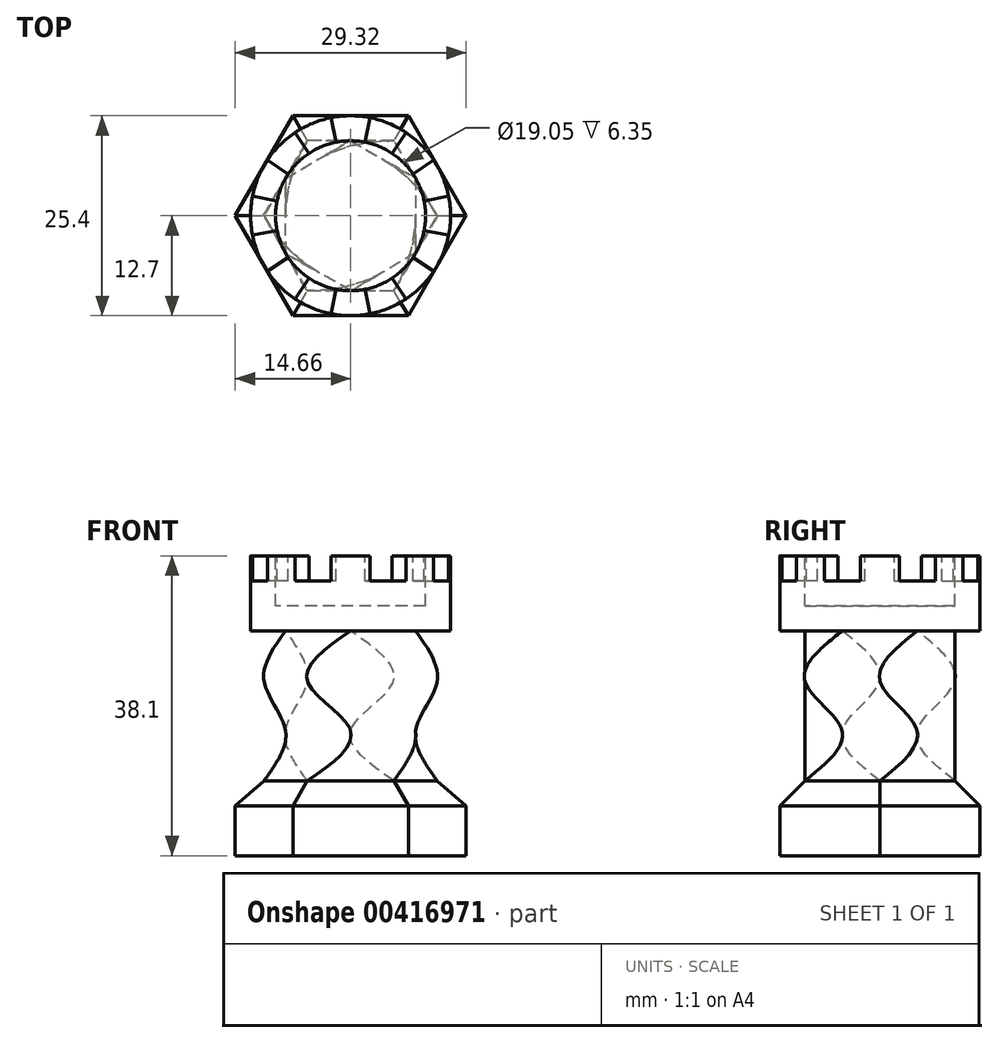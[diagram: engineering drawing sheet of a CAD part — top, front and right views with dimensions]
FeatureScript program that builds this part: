
annotation { "Feature Type Name" : "Feature", "Feature Type Description" : "" }
export const myFeature = defineFeature(function(context is Context, id is Id, definition is map)
    precondition{}
    {
        {
            var Q0;
            Q0=qCreatedBy(makeId("Top.planeOp"),FACE);
            var sketch = newSketch(context, id + "F0", { "sketchPlane" : qUnion([Q0])});
            skCircle(sketch, "E0.cCircle", {"center": v(0, 0) * mm, "radius": 12.7 * mm, "construction": true});
            skLineSegment(sketch, "E0.0", {"start": v(-7.33, 12.7) * mm, "end": v(7.33, 12.7) * mm});
            skLineSegment(sketch, "E0.1", {"start": v(7.33, 12.7) * mm, "end": v(14.66, 0) * mm});
            skLineSegment(sketch, "E0.2", {"start": v(14.66, 0) * mm, "end": v(7.33, -12.7) * mm});
            skLineSegment(sketch, "E0.3", {"start": v(7.33, -12.7) * mm, "end": v(-7.33, -12.7) * mm});
            skLineSegment(sketch, "E0.4", {"start": v(-7.33, -12.7) * mm, "end": v(-14.66, 0) * mm});
            skLineSegment(sketch, "E0.5", {"start": v(-14.66, 0) * mm, "end": v(-7.33, 12.7) * mm});
            skPoint(sketch, "E0.0.midPoint", {"position": v(0, 12.7) * mm});
            skSolve(sketch);
        }
        {
            var Q0;
            Q0=makeQuery(id+"F0.imprint","IMPRINT",FACE,{"disambiguationData":[TD([[makeQuery(id+"F0.imprint","IMPRINT",EDGE,{"derivedFrom":sQuery(id+"F0.wireOp",EDGE,"E0.0")}),-1.0]])]});
            extrude(context, id + "F1", {"entities" : qUnion([Q0]), "depth" : 9.52 * mm, "offsetDistance" : 25.4 * mm});
        }
        {
            var Q0;
            Q0=makeQuery(id+"F1.opExtrude","CAP_EDGE",EDGE,{"disambiguationData":[OSD([sQuery(id+"F0.wireOp",EDGE,"E0.3")])],"isStart":false});
            var Q1;
            Q1=makeQuery(id+"F1.opExtrude","CAP_EDGE",EDGE,{"disambiguationData":[OSD([sQuery(id+"F0.wireOp",EDGE,"E0.2")])],"isStart":false});
            var Q2;
            Q2=makeQuery(id+"F1.opExtrude","CAP_EDGE",EDGE,{"disambiguationData":[OSD([sQuery(id+"F0.wireOp",EDGE,"E0.1")])],"isStart":false});
            var Q3;
            Q3=makeQuery(id+"F1.opExtrude","CAP_EDGE",EDGE,{"disambiguationData":[OSD([sQuery(id+"F0.wireOp",EDGE,"E0.0")])],"isStart":false});
            var Q4;
            Q4=makeQuery(id+"F1.opExtrude","CAP_EDGE",EDGE,{"disambiguationData":[OSD([sQuery(id+"F0.wireOp",EDGE,"E0.5")])],"isStart":false});
            var Q5;
            Q5=makeQuery(id+"F1.opExtrude","CAP_EDGE",EDGE,{"disambiguationData":[OSD([sQuery(id+"F0.wireOp",EDGE,"E0.4")])],"isStart":false});
            chamfer(context, id + "F2", {"entities" : qUnion([Q0, Q1, Q2, Q3, Q4, Q5]), "width" : 3.17 * mm, "tangentPropagation" : true});
        }
        {
            var Q0;
            Q0=makeQuery(id+"F1.opExtrude","CAP_FACE",FACE,{"disambiguationData":[OSD([sQuery(id+"F0.wireOp",EDGE,"E0.0"),sQuery(id+"F0.wireOp",EDGE,"E0.1"),sQuery(id+"F0.wireOp",EDGE,"E0.2"),sQuery(id+"F0.wireOp",EDGE,"E0.3"),sQuery(id+"F0.wireOp",EDGE,"E0.4"),sQuery(id+"F0.wireOp",EDGE,"E0.5")])],"isStart":false});
            cPlane(context, id + "F3", {"entities" : qUnion([Q0]), "cplaneType" : CPlaneType.OFFSET, "offset" : 6.35 * mm, "width" : 152.4 * mm, "height" : 152.4 * mm});
        }
        {
            var Q0;
            Q0=qCreatedBy(id+"F3.planeOp",FACE);
            var sketch = newSketch(context, id + "F4", { "sketchPlane" : qUnion([Q0])});
            skCircle(sketch, "E1.cCircle", {"center": v(0, 0) * mm, "radius": 8.25 * mm, "construction": true});
            skLineSegment(sketch, "E1.0", {"start": v(8.25, -4.76) * mm, "end": v(0, -9.53) * mm});
            skLineSegment(sketch, "E1.1", {"start": v(0, -9.52) * mm, "end": v(-8.25, -4.76) * mm});
            skLineSegment(sketch, "E1.2", {"start": v(-8.25, -4.76) * mm, "end": v(-8.25, 4.76) * mm});
            skLineSegment(sketch, "E1.3", {"start": v(-8.25, 4.76) * mm, "end": v(0, 9.52) * mm});
            skLineSegment(sketch, "E1.4", {"start": v(0, 9.52) * mm, "end": v(8.25, 4.76) * mm});
            skLineSegment(sketch, "E1.5", {"start": v(8.25, 4.76) * mm, "end": v(8.25, -4.76) * mm});
            skPoint(sketch, "E1.0.midPoint", {"position": v(4.12, -7.14) * mm});
            skSolve(sketch);
        }
        {
            var Q0;
            Q0=makeQuery(id+"F4.imprint","IMPRINT",FACE,{"disambiguationData":[TD([[makeQuery(id+"F4.imprint","IMPRINT",EDGE,{"derivedFrom":sQuery(id+"F4.wireOp",EDGE,"E1.0")}),-1.0]])]});
            cPlane(context, id + "F5", {"entities" : qUnion([Q0]), "cplaneType" : CPlaneType.OFFSET, "offset" : 6.35 * mm, "width" : 152.4 * mm, "height" : 152.4 * mm});
        }
        {
            var Q0;
            Q0=qCreatedBy(id+"F5.planeOp",FACE);
            var sketch = newSketch(context, id + "F6", { "sketchPlane" : qUnion([Q0])});
            skCircle(sketch, "E2.cCircle", {"center": v(0, 0) * mm, "radius": 9.52 * mm, "construction": true});
            skLineSegment(sketch, "E2.0", {"start": v(-5.5, 9.52) * mm, "end": v(5.5, 9.52) * mm});
            skLineSegment(sketch, "E2.1", {"start": v(5.5, 9.53) * mm, "end": v(11, 0) * mm});
            skLineSegment(sketch, "E2.2", {"start": v(11, 0) * mm, "end": v(5.5, -9.53) * mm});
            skLineSegment(sketch, "E2.3", {"start": v(5.5, -9.52) * mm, "end": v(-5.5, -9.52) * mm});
            skLineSegment(sketch, "E2.4", {"start": v(-5.5, -9.53) * mm, "end": v(-11, 0) * mm});
            skLineSegment(sketch, "E2.5", {"start": v(-11, 0) * mm, "end": v(-5.5, 9.53) * mm});
            skPoint(sketch, "E2.0.midPoint", {"position": v(0, 9.52) * mm});
            skSolve(sketch);
        }
        {
            var Q0;
            Q0=makeQuery(id+"F6.imprint","IMPRINT",FACE,{"disambiguationData":[TD([[makeQuery(id+"F6.imprint","IMPRINT",EDGE,{"derivedFrom":sQuery(id+"F6.wireOp",EDGE,"E2.0")}),-1.0]])]});
            cPlane(context, id + "F7", {"entities" : qUnion([Q0]), "cplaneType" : CPlaneType.OFFSET, "offset" : 6.35 * mm, "width" : 152.4 * mm, "height" : 152.4 * mm});
        }
        {
            var Q0;
            Q0=qCreatedBy(id+"F7.planeOp",FACE);
            var sketch = newSketch(context, id + "F8", { "sketchPlane" : qUnion([Q0])});
            skCircle(sketch, "E3.cCircle", {"center": v(0, 0) * mm, "radius": 8.25 * mm, "construction": true});
            skLineSegment(sketch, "E3.0", {"start": v(-8.25, 4.76) * mm, "end": v(0, 9.53) * mm});
            skLineSegment(sketch, "E3.1", {"start": v(0, 9.52) * mm, "end": v(8.25, 4.76) * mm});
            skLineSegment(sketch, "E3.2", {"start": v(8.25, 4.76) * mm, "end": v(8.25, -4.76) * mm});
            skLineSegment(sketch, "E3.3", {"start": v(8.25, -4.76) * mm, "end": v(0, -9.53) * mm});
            skLineSegment(sketch, "E3.4", {"start": v(0, -9.53) * mm, "end": v(-8.25, -4.76) * mm});
            skLineSegment(sketch, "E3.5", {"start": v(-8.25, -4.76) * mm, "end": v(-8.25, 4.76) * mm});
            skPoint(sketch, "E3.0.midPoint", {"position": v(-4.12, 7.14) * mm});
            skSolve(sketch);
        }
        {
            var Q1;
            Q1=makeQuery(id+"F1.opExtrude","CAP_FACE",FACE,{"disambiguationData":[OSD([sQuery(id+"F0.wireOp",EDGE,"E0.0"),sQuery(id+"F0.wireOp",EDGE,"E0.1"),sQuery(id+"F0.wireOp",EDGE,"E0.2"),sQuery(id+"F0.wireOp",EDGE,"E0.3"),sQuery(id+"F0.wireOp",EDGE,"E0.4"),sQuery(id+"F0.wireOp",EDGE,"E0.5")])],"isStart":false});
            var Q2;
            Q2=makeQuery(id+"F4.imprint","IMPRINT",FACE,{"disambiguationData":[TD([[makeQuery(id+"F4.imprint","IMPRINT",EDGE,{"derivedFrom":sQuery(id+"F4.wireOp",EDGE,"E1.0")}),-1.0]])]});
            var Q3;
            Q3=makeQuery(id+"F6.imprint","IMPRINT",FACE,{"disambiguationData":[TD([[makeQuery(id+"F6.imprint","IMPRINT",EDGE,{"derivedFrom":sQuery(id+"F6.wireOp",EDGE,"E2.0")}),-1.0]])]});
            var Q4;
            Q4=makeQuery(id+"F8.imprint","IMPRINT",FACE,{"disambiguationData":[TD([[makeQuery(id+"F8.imprint","IMPRINT",EDGE,{"derivedFrom":sQuery(id+"F8.wireOp",EDGE,"E3.0")}),-1.0]])]});
            loft(context, id + "F9", {"operationType" : NewBodyOperationType.ADD, "sheetProfilesArray" : [{ "sheetProfileEntities" : qUnion([Q1]) }, { "sheetProfileEntities" : qUnion([Q2]) }, { "sheetProfileEntities" : qUnion([Q3]) }, { "sheetProfileEntities" : qUnion([Q4]) }]});
        }
        {
            var Q0;
            Q0=makeQuery(id+"F9.opLoft","CAP_FACE",FACE,{"disambiguationData":[OSD([makeQuery(id+"F8.imprint","IMPRINT",FACE,{"disambiguationData":[TD([[makeQuery(id+"F8.imprint","IMPRINT",EDGE,{"derivedFrom":sQuery(id+"F8.wireOp",EDGE,"E3.0")}),-1.0]])]})])],"isStart":true});
            var sketch = newSketch(context, id + "F10", { "sketchPlane" : qUnion([Q0])});
            skCircle(sketch, "E4", {"center": v(0, 0) * mm, "radius": 12.7 * mm});
            skCircle(sketch, "E5", {"center": v(0, 0) * mm, "radius": 9.53 * mm});
            skSolve(sketch);
        }
        {
            var Q0;
            Q0=makeQuery(id+"F10.imprint","IMPRINT",FACE,{"disambiguationData":[TD([[makeQuery(id+"F10.imprint","IMPRINT",EDGE,{"derivedFrom":sQuery(id+"F10.wireOp",EDGE,"E4")}),1.0]])]});
            var Q1;
            {var subQ2=sQuery(id+"F8.wireOp",EDGE,"E3.1");var subQ3=sQuery(id+"F8.wireOp",EDGE,"E3.0");var subQ4=sQuery(id+"F8.wireOp",EDGE,"E3.5");Q1=makeQuery(id+"F10.imprint","IMPRINT",FACE,{"disambiguationData":[TD([[makeQuery(id+"F10.imprint","IMPRINT",EDGE,{"derivedFrom":makeQuery(id+"F9.opLoft","MID_CAP_EDGE",EDGE,{"disambiguationData":[OSD([subQ3,subQ2,subQ4])],"capPos":3.0})}),1.0]])]});}
            var Q2;
            {var subQ1=sQuery(id+"F8.wireOp",EDGE,"E3.5");var subQ2=sQuery(id+"F8.wireOp",EDGE,"E3.0");var subQ3=sQuery(id+"F8.wireOp",EDGE,"E3.1");var subQ4=makeQuery(id+"F9.opLoft","MID_CAP_EDGE",EDGE,{"disambiguationData":[OSD([subQ2,subQ3,subQ1])],"capPos":3.0});Q2=makeQuery(id+"F10.imprint","IMPRINT",FACE,{"disambiguationData":[TD([[makeQuery(id+"F10.imprint","IMPRINT",EDGE,{"derivedFrom":subQ4}),-1.0]])]});}
            var Q3;
            {var subQ1=sQuery(id+"F8.wireOp",EDGE,"E3.2");var subQ2=sQuery(id+"F8.wireOp",EDGE,"E3.1");var subQ3=sQuery(id+"F8.wireOp",EDGE,"E3.0");var subQ4=makeQuery(id+"F9.opLoft","MID_CAP_EDGE",EDGE,{"disambiguationData":[OSD([subQ3,subQ2,subQ1])],"capPos":3.0});Q3=makeQuery(id+"F10.imprint","IMPRINT",FACE,{"disambiguationData":[TD([[makeQuery(id+"F10.imprint","IMPRINT",EDGE,{"derivedFrom":subQ4}),-1.0]])]});}
            var Q4;
            {var subQ1=sQuery(id+"F8.wireOp",EDGE,"E3.5");var subQ2=sQuery(id+"F8.wireOp",EDGE,"E3.4");var subQ3=sQuery(id+"F8.wireOp",EDGE,"E3.0");var subQ4=makeQuery(id+"F9.opLoft","MID_CAP_EDGE",EDGE,{"disambiguationData":[OSD([subQ3,subQ2,subQ1])],"capPos":3.0});Q4=makeQuery(id+"F10.imprint","IMPRINT",FACE,{"disambiguationData":[TD([[makeQuery(id+"F10.imprint","IMPRINT",EDGE,{"derivedFrom":subQ4}),-1.0]])]});}
            var Q5;
            {var subQ1=sQuery(id+"F8.wireOp",EDGE,"E3.5");var subQ2=sQuery(id+"F8.wireOp",EDGE,"E3.4");var subQ3=sQuery(id+"F8.wireOp",EDGE,"E3.3");var subQ4=makeQuery(id+"F9.opLoft","MID_CAP_EDGE",EDGE,{"disambiguationData":[OSD([subQ3,subQ2,subQ1])],"capPos":3.0});Q5=makeQuery(id+"F10.imprint","IMPRINT",FACE,{"disambiguationData":[TD([[makeQuery(id+"F10.imprint","IMPRINT",EDGE,{"derivedFrom":subQ4}),-1.0]])]});}
            var Q6;
            {var subQ1=sQuery(id+"F8.wireOp",EDGE,"E3.3");var subQ2=sQuery(id+"F8.wireOp",EDGE,"E3.2");var subQ3=sQuery(id+"F8.wireOp",EDGE,"E3.1");var subQ4=makeQuery(id+"F9.opLoft","MID_CAP_EDGE",EDGE,{"disambiguationData":[OSD([subQ3,subQ2,subQ1])],"capPos":3.0});Q6=makeQuery(id+"F10.imprint","IMPRINT",FACE,{"disambiguationData":[TD([[makeQuery(id+"F10.imprint","IMPRINT",EDGE,{"derivedFrom":subQ4}),-1.0]])]});}
            var Q7;
            {var subQ1=sQuery(id+"F8.wireOp",EDGE,"E3.4");var subQ2=sQuery(id+"F8.wireOp",EDGE,"E3.3");var subQ3=sQuery(id+"F8.wireOp",EDGE,"E3.2");var subQ4=makeQuery(id+"F9.opLoft","MID_CAP_EDGE",EDGE,{"disambiguationData":[OSD([subQ3,subQ2,subQ1])],"capPos":3.0});Q7=makeQuery(id+"F10.imprint","IMPRINT",FACE,{"disambiguationData":[TD([[makeQuery(id+"F10.imprint","IMPRINT",EDGE,{"derivedFrom":subQ4}),-1.0]])]});}
            extrude(context, id + "F11", {"entities" : qUnion([Q0, Q1, Q2, Q3, Q4, Q5, Q6, Q7]), "operationType" : NewBodyOperationType.ADD, "depth" : 9.52 * mm, "offsetDistance" : 25.4 * mm});
        }
        {
            var Q0;
            Q0=makeQuery(id+"F11.opExtrude","CAP_FACE",FACE,{"disambiguationData":[OSD([sQuery(id+"F10.wireOp",EDGE,"E4")])],"isStart":false});
            var sketch = newSketch(context, id + "F12", { "sketchPlane" : qUnion([Q0])});
            skCircle(sketch, "E6", {"center": v(0, 0) * mm, "radius": 9.53 * mm});
            skLineSegment(sketch, "E7", {"start": v(0, 0) * mm, "end": v(0, 12.7) * mm});
            skLineSegment(sketch, "E8", {"start": v(0, 0) * mm, "end": v(12.7, 0) * mm});
            skLineSegment(sketch, "E9", {"start": v(0, 0) * mm, "end": v(-12.7, 0) * mm});
            skLineSegment(sketch, "E10", {"start": v(0, 0) * mm, "end": v(0, -12.7) * mm});
            skLineSegment(sketch, "E11", {"start": v(0, 0) * mm, "end": v(-8.98, 8.98) * mm});
            skLineSegment(sketch, "E12", {"start": v(0, 0) * mm, "end": v(8.98, -8.98) * mm});
            skLineSegment(sketch, "E13", {"start": v(0, 0) * mm, "end": v(8.98, 8.98) * mm});
            skLineSegment(sketch, "E14", {"start": v(0, 0) * mm, "end": v(-8.98, -8.98) * mm});
            skLineSegment(sketch, "E15", {"start": v(0, 0) * mm, "end": v(-4.86, 11.73) * mm});
            skLineSegment(sketch, "E16", {"start": v(0, 0) * mm, "end": v(4.86, 11.73) * mm});
            skLineSegment(sketch, "E17", {"start": v(0, 0) * mm, "end": v(11.73, 4.86) * mm});
            skLineSegment(sketch, "E18", {"start": v(0, 0) * mm, "end": v(11.73, -4.86) * mm});
            skLineSegment(sketch, "E19", {"start": v(0, 0) * mm, "end": v(4.86, -11.73) * mm});
            skLineSegment(sketch, "E20", {"start": v(0, 0) * mm, "end": v(-4.86, -11.73) * mm});
            skLineSegment(sketch, "E21", {"start": v(0, 0) * mm, "end": v(-11.73, 4.86) * mm});
            skLineSegment(sketch, "E22", {"start": v(0, 0) * mm, "end": v(-11.73, -4.86) * mm});
            skLineSegment(sketch, "E23", {"start": v(0, 0) * mm, "end": v(-2.48, 12.46) * mm});
            skLineSegment(sketch, "E24", {"start": v(0, 0) * mm, "end": v(2.48, 12.46) * mm});
            skLineSegment(sketch, "E25", {"start": v(0, 0) * mm, "end": v(7.06, 10.56) * mm});
            skLineSegment(sketch, "E26", {"start": v(0, 0) * mm, "end": v(10.56, 7.06) * mm});
            skLineSegment(sketch, "E27", {"start": v(0, 0) * mm, "end": v(12.46, 2.48) * mm});
            skLineSegment(sketch, "E28", {"start": v(0, 0) * mm, "end": v(12.46, -2.48) * mm});
            skLineSegment(sketch, "E29", {"start": v(0, 0) * mm, "end": v(10.56, -7.06) * mm});
            skLineSegment(sketch, "E30", {"start": v(0, 0) * mm, "end": v(7.06, -10.56) * mm});
            skLineSegment(sketch, "E31", {"start": v(0, 0) * mm, "end": v(2.48, -12.46) * mm});
            skLineSegment(sketch, "E32", {"start": v(0, 0) * mm, "end": v(-7.06, 10.56) * mm});
            skLineSegment(sketch, "E33", {"start": v(0, 0) * mm, "end": v(-10.56, 7.06) * mm});
            skLineSegment(sketch, "E34", {"start": v(0, 0) * mm, "end": v(-12.46, 2.48) * mm});
            skLineSegment(sketch, "E35", {"start": v(0, 0) * mm, "end": v(-12.46, -2.48) * mm});
            skLineSegment(sketch, "E36", {"start": v(0, 0) * mm, "end": v(-10.56, -7.06) * mm});
            skLineSegment(sketch, "E37", {"start": v(0, 0) * mm, "end": v(-2.48, -12.46) * mm});
            skLineSegment(sketch, "E38", {"start": v(0, 0) * mm, "end": v(-7.06, -10.56) * mm});
            skSolve(sketch);
        }
        {
            var Q0;
            {var subQ0=sQuery(id+"F12.wireOp",EDGE,"E16");var subQ1=sQuery(id+"F12.wireOp",EDGE,"E6");var subQ2=makeQuery(id+"F12.imprint","INTERSECT",VERTEX,{"derivedFrom":[subQ1,subQ0]});Q0=makeQuery(id+"F12.imprint","IMPRINT",FACE,{"disambiguationData":[TD([[makeQuery(id+"F12.imprint","IMPRINT",EDGE,{"disambiguationData":[TD([[subQ2,-1.0]])],"derivedFrom":subQ1}),-1.0]])]});}
            var Q1;
            {var subQ0=sQuery(id+"F12.wireOp",EDGE,"E25");var subQ1=sQuery(id+"F12.wireOp",EDGE,"E6");var subQ2=makeQuery(id+"F12.imprint","INTERSECT",VERTEX,{"derivedFrom":[subQ1,subQ0]});Q1=makeQuery(id+"F12.imprint","IMPRINT",FACE,{"disambiguationData":[TD([[makeQuery(id+"F12.imprint","IMPRINT",EDGE,{"disambiguationData":[TD([[subQ2,-1.0]])],"derivedFrom":subQ1}),-1.0]])]});}
            var Q2;
            {var subQ0=sQuery(id+"F12.wireOp",EDGE,"E17");var subQ1=sQuery(id+"F12.wireOp",EDGE,"E6");var subQ2=makeQuery(id+"F12.imprint","INTERSECT",VERTEX,{"derivedFrom":[subQ1,subQ0]});Q2=makeQuery(id+"F12.imprint","IMPRINT",FACE,{"disambiguationData":[TD([[makeQuery(id+"F12.imprint","IMPRINT",EDGE,{"disambiguationData":[TD([[subQ2,-1.0]])],"derivedFrom":subQ1}),-1.0]])]});}
            var Q3;
            {var subQ0=sQuery(id+"F12.wireOp",EDGE,"E27");var subQ1=sQuery(id+"F12.wireOp",EDGE,"E6");var subQ2=makeQuery(id+"F12.imprint","INTERSECT",VERTEX,{"derivedFrom":[subQ1,subQ0]});Q3=makeQuery(id+"F12.imprint","IMPRINT",FACE,{"disambiguationData":[TD([[makeQuery(id+"F12.imprint","IMPRINT",EDGE,{"disambiguationData":[TD([[subQ2,-1.0]])],"derivedFrom":subQ1}),-1.0]])]});}
            var Q4;
            {var subQ0=sQuery(id+"F12.wireOp",EDGE,"E18");var subQ1=sQuery(id+"F12.wireOp",EDGE,"E6");var subQ2=makeQuery(id+"F12.imprint","INTERSECT",VERTEX,{"derivedFrom":[subQ1,subQ0]});Q4=makeQuery(id+"F12.imprint","IMPRINT",FACE,{"disambiguationData":[TD([[makeQuery(id+"F12.imprint","IMPRINT",EDGE,{"disambiguationData":[TD([[subQ2,-1.0]])],"derivedFrom":subQ1}),-1.0]])]});}
            var Q5;
            {var subQ0=sQuery(id+"F12.wireOp",EDGE,"E29");var subQ1=sQuery(id+"F12.wireOp",EDGE,"E6");var subQ2=makeQuery(id+"F12.imprint","INTERSECT",VERTEX,{"derivedFrom":[subQ1,subQ0]});Q5=makeQuery(id+"F12.imprint","IMPRINT",FACE,{"disambiguationData":[TD([[makeQuery(id+"F12.imprint","IMPRINT",EDGE,{"disambiguationData":[TD([[subQ2,-1.0]])],"derivedFrom":subQ1}),-1.0]])]});}
            var Q6;
            {var subQ0=sQuery(id+"F12.wireOp",EDGE,"E19");var subQ1=sQuery(id+"F12.wireOp",EDGE,"E6");var subQ2=makeQuery(id+"F12.imprint","INTERSECT",VERTEX,{"derivedFrom":[subQ1,subQ0]});Q6=makeQuery(id+"F12.imprint","IMPRINT",FACE,{"disambiguationData":[TD([[makeQuery(id+"F12.imprint","IMPRINT",EDGE,{"disambiguationData":[TD([[subQ2,-1.0]])],"derivedFrom":subQ1}),-1.0]])]});}
            var Q7;
            {var subQ0=sQuery(id+"F12.wireOp",EDGE,"E31");var subQ1=sQuery(id+"F12.wireOp",EDGE,"E6");var subQ2=makeQuery(id+"F12.imprint","INTERSECT",VERTEX,{"derivedFrom":[subQ1,subQ0]});Q7=makeQuery(id+"F12.imprint","IMPRINT",FACE,{"disambiguationData":[TD([[makeQuery(id+"F12.imprint","IMPRINT",EDGE,{"disambiguationData":[TD([[subQ2,-1.0]])],"derivedFrom":subQ1}),-1.0]])]});}
            var Q8;
            {var subQ0=sQuery(id+"F12.wireOp",EDGE,"E20");var subQ1=sQuery(id+"F12.wireOp",EDGE,"E6");var subQ2=makeQuery(id+"F12.imprint","INTERSECT",VERTEX,{"derivedFrom":[subQ1,subQ0]});Q8=makeQuery(id+"F12.imprint","IMPRINT",FACE,{"disambiguationData":[TD([[makeQuery(id+"F12.imprint","IMPRINT",EDGE,{"disambiguationData":[TD([[subQ2,-1.0]])],"derivedFrom":subQ1}),-1.0]])]});}
            var Q9;
            {var subQ0=sQuery(id+"F12.wireOp",EDGE,"E38");var subQ1=sQuery(id+"F12.wireOp",EDGE,"E6");var subQ2=makeQuery(id+"F12.imprint","INTERSECT",VERTEX,{"derivedFrom":[subQ1,subQ0]});Q9=makeQuery(id+"F12.imprint","IMPRINT",FACE,{"disambiguationData":[TD([[makeQuery(id+"F12.imprint","IMPRINT",EDGE,{"disambiguationData":[TD([[subQ2,-1.0]])],"derivedFrom":subQ1}),-1.0]])]});}
            var Q10;
            {var subQ0=sQuery(id+"F12.wireOp",EDGE,"E22");var subQ1=sQuery(id+"F12.wireOp",EDGE,"E6");var subQ2=makeQuery(id+"F12.imprint","INTERSECT",VERTEX,{"derivedFrom":[subQ1,subQ0]});Q10=makeQuery(id+"F12.imprint","IMPRINT",FACE,{"disambiguationData":[TD([[makeQuery(id+"F12.imprint","IMPRINT",EDGE,{"disambiguationData":[TD([[subQ2,-1.0]])],"derivedFrom":subQ1}),-1.0]])]});}
            var Q11;
            {var subQ0=sQuery(id+"F12.wireOp",EDGE,"E35");var subQ1=sQuery(id+"F12.wireOp",EDGE,"E6");var subQ2=makeQuery(id+"F12.imprint","INTERSECT",VERTEX,{"derivedFrom":[subQ1,subQ0]});Q11=makeQuery(id+"F12.imprint","IMPRINT",FACE,{"disambiguationData":[TD([[makeQuery(id+"F12.imprint","IMPRINT",EDGE,{"disambiguationData":[TD([[subQ2,-1.0]])],"derivedFrom":subQ1}),-1.0]])]});}
            var Q12;
            {var subQ0=sQuery(id+"F12.wireOp",EDGE,"E15");var subQ1=sQuery(id+"F12.wireOp",EDGE,"E6");var subQ2=makeQuery(id+"F12.imprint","INTERSECT",VERTEX,{"derivedFrom":[subQ1,subQ0]});Q12=makeQuery(id+"F12.imprint","IMPRINT",FACE,{"disambiguationData":[TD([[makeQuery(id+"F12.imprint","IMPRINT",EDGE,{"disambiguationData":[TD([[subQ2,-1.0]])],"derivedFrom":subQ1}),-1.0]])]});}
            var Q13;
            {var subQ0=sQuery(id+"F12.wireOp",EDGE,"E23");var subQ1=sQuery(id+"F12.wireOp",EDGE,"E6");var subQ2=makeQuery(id+"F12.imprint","INTERSECT",VERTEX,{"derivedFrom":[subQ1,subQ0]});Q13=makeQuery(id+"F12.imprint","IMPRINT",FACE,{"disambiguationData":[TD([[makeQuery(id+"F12.imprint","IMPRINT",EDGE,{"disambiguationData":[TD([[subQ2,-1.0]])],"derivedFrom":subQ1}),-1.0]])]});}
            var Q14;
            {var subQ0=sQuery(id+"F12.wireOp",EDGE,"E33");var subQ1=sQuery(id+"F12.wireOp",EDGE,"E6");var subQ2=makeQuery(id+"F12.imprint","INTERSECT",VERTEX,{"derivedFrom":[subQ1,subQ0]});Q14=makeQuery(id+"F12.imprint","IMPRINT",FACE,{"disambiguationData":[TD([[makeQuery(id+"F12.imprint","IMPRINT",EDGE,{"disambiguationData":[TD([[subQ2,-1.0]])],"derivedFrom":subQ1}),-1.0]])]});}
            var Q15;
            {var subQ0=sQuery(id+"F12.wireOp",EDGE,"E21");var subQ1=sQuery(id+"F12.wireOp",EDGE,"E6");var subQ2=makeQuery(id+"F12.imprint","INTERSECT",VERTEX,{"derivedFrom":[subQ1,subQ0]});Q15=makeQuery(id+"F12.imprint","IMPRINT",FACE,{"disambiguationData":[TD([[makeQuery(id+"F12.imprint","IMPRINT",EDGE,{"disambiguationData":[TD([[subQ2,-1.0]])],"derivedFrom":subQ1}),-1.0]])]});}
            var Q16;
            {var subQ0=sQuery(id+"F12.wireOp",EDGE,"E32");var subQ1=sQuery(id+"F12.wireOp",EDGE,"E6");var subQ2=makeQuery(id+"F12.imprint","INTERSECT",VERTEX,{"derivedFrom":[subQ1,subQ0]});Q16=makeQuery(id+"F12.imprint","IMPRINT",FACE,{"disambiguationData":[TD([[makeQuery(id+"F12.imprint","IMPRINT",EDGE,{"disambiguationData":[TD([[subQ2,-1.0]])],"derivedFrom":subQ1}),1.0]])]});}
            var Q17;
            {var subQ0=sQuery(id+"F12.wireOp",EDGE,"E15");var subQ1=sQuery(id+"F12.wireOp",EDGE,"E6");var subQ2=makeQuery(id+"F12.imprint","INTERSECT",VERTEX,{"derivedFrom":[subQ1,subQ0]});Q17=makeQuery(id+"F12.imprint","IMPRINT",FACE,{"disambiguationData":[TD([[makeQuery(id+"F12.imprint","IMPRINT",EDGE,{"disambiguationData":[TD([[subQ2,-1.0]])],"derivedFrom":subQ1}),1.0]])]});}
            var Q18;
            {var subQ0=sQuery(id+"F12.wireOp",EDGE,"E24");var subQ1=sQuery(id+"F12.wireOp",EDGE,"E6");var subQ2=makeQuery(id+"F12.imprint","INTERSECT",VERTEX,{"derivedFrom":[subQ1,subQ0]});Q18=makeQuery(id+"F12.imprint","IMPRINT",FACE,{"disambiguationData":[TD([[makeQuery(id+"F12.imprint","IMPRINT",EDGE,{"disambiguationData":[TD([[subQ2,-1.0]])],"derivedFrom":subQ1}),1.0]])]});}
            var Q19;
            {var subQ0=sQuery(id+"F12.wireOp",EDGE,"E7");var subQ1=sQuery(id+"F12.wireOp",EDGE,"E6");var subQ2=makeQuery(id+"F12.imprint","INTERSECT",VERTEX,{"derivedFrom":[subQ1,subQ0]});Q19=makeQuery(id+"F12.imprint","IMPRINT",FACE,{"disambiguationData":[TD([[makeQuery(id+"F12.imprint","IMPRINT",EDGE,{"disambiguationData":[TD([[subQ2,-1.0]])],"derivedFrom":subQ1}),1.0]])]});}
            var Q20;
            {var subQ0=sQuery(id+"F12.wireOp",EDGE,"E16");var subQ1=sQuery(id+"F12.wireOp",EDGE,"E6");var subQ2=makeQuery(id+"F12.imprint","INTERSECT",VERTEX,{"derivedFrom":[subQ1,subQ0]});Q20=makeQuery(id+"F12.imprint","IMPRINT",FACE,{"disambiguationData":[TD([[makeQuery(id+"F12.imprint","IMPRINT",EDGE,{"disambiguationData":[TD([[subQ2,-1.0]])],"derivedFrom":subQ1}),1.0]])]});}
            var Q21;
            {var subQ0=sQuery(id+"F12.wireOp",EDGE,"E25");var subQ1=sQuery(id+"F12.wireOp",EDGE,"E6");var subQ2=makeQuery(id+"F12.imprint","INTERSECT",VERTEX,{"derivedFrom":[subQ1,subQ0]});Q21=makeQuery(id+"F12.imprint","IMPRINT",FACE,{"disambiguationData":[TD([[makeQuery(id+"F12.imprint","IMPRINT",EDGE,{"disambiguationData":[TD([[subQ2,-1.0]])],"derivedFrom":subQ1}),1.0]])]});}
            var Q22;
            {var subQ0=sQuery(id+"F12.wireOp",EDGE,"E13");var subQ1=sQuery(id+"F12.wireOp",EDGE,"E6");var subQ2=makeQuery(id+"F12.imprint","INTERSECT",VERTEX,{"derivedFrom":[subQ1,subQ0]});Q22=makeQuery(id+"F12.imprint","IMPRINT",FACE,{"disambiguationData":[TD([[makeQuery(id+"F12.imprint","IMPRINT",EDGE,{"disambiguationData":[TD([[subQ2,-1.0]])],"derivedFrom":subQ1}),1.0]])]});}
            var Q23;
            {var subQ0=sQuery(id+"F12.wireOp",EDGE,"E26");var subQ1=sQuery(id+"F12.wireOp",EDGE,"E6");var subQ2=makeQuery(id+"F12.imprint","INTERSECT",VERTEX,{"derivedFrom":[subQ1,subQ0]});Q23=makeQuery(id+"F12.imprint","IMPRINT",FACE,{"disambiguationData":[TD([[makeQuery(id+"F12.imprint","IMPRINT",EDGE,{"disambiguationData":[TD([[subQ2,-1.0]])],"derivedFrom":subQ1}),1.0]])]});}
            var Q24;
            {var subQ0=sQuery(id+"F12.wireOp",EDGE,"E17");var subQ1=sQuery(id+"F12.wireOp",EDGE,"E6");var subQ2=makeQuery(id+"F12.imprint","INTERSECT",VERTEX,{"derivedFrom":[subQ1,subQ0]});Q24=makeQuery(id+"F12.imprint","IMPRINT",FACE,{"disambiguationData":[TD([[makeQuery(id+"F12.imprint","IMPRINT",EDGE,{"disambiguationData":[TD([[subQ2,-1.0]])],"derivedFrom":subQ1}),1.0]])]});}
            var Q25;
            {var subQ0=sQuery(id+"F12.wireOp",EDGE,"E27");var subQ1=sQuery(id+"F12.wireOp",EDGE,"E6");var subQ2=makeQuery(id+"F12.imprint","INTERSECT",VERTEX,{"derivedFrom":[subQ1,subQ0]});Q25=makeQuery(id+"F12.imprint","IMPRINT",FACE,{"disambiguationData":[TD([[makeQuery(id+"F12.imprint","IMPRINT",EDGE,{"disambiguationData":[TD([[subQ2,-1.0]])],"derivedFrom":subQ1}),1.0]])]});}
            var Q26;
            {var subQ0=sQuery(id+"F12.wireOp",EDGE,"E27");var subQ1=sQuery(id+"F12.wireOp",EDGE,"E6");var subQ2=makeQuery(id+"F12.imprint","INTERSECT",VERTEX,{"derivedFrom":[subQ1,subQ0]});Q26=makeQuery(id+"F12.imprint","IMPRINT",FACE,{"disambiguationData":[TD([[makeQuery(id+"F12.imprint","IMPRINT",EDGE,{"disambiguationData":[TD([[subQ2,1.0]])],"derivedFrom":subQ1}),1.0]])]});}
            var Q27;
            {var subQ0=sQuery(id+"F12.wireOp",EDGE,"E8");var subQ1=sQuery(id+"F12.wireOp",EDGE,"E6");var subQ2=makeQuery(id+"F12.imprint","INTERSECT",VERTEX,{"derivedFrom":[subQ1,subQ0]});Q27=makeQuery(id+"F12.imprint","IMPRINT",FACE,{"disambiguationData":[TD([[makeQuery(id+"F12.imprint","IMPRINT",EDGE,{"disambiguationData":[TD([[subQ2,1.0]])],"derivedFrom":subQ1}),1.0]])]});}
            var Q28;
            {var subQ0=sQuery(id+"F12.wireOp",EDGE,"E18");var subQ1=sQuery(id+"F12.wireOp",EDGE,"E6");var subQ2=makeQuery(id+"F12.imprint","INTERSECT",VERTEX,{"derivedFrom":[subQ1,subQ0]});Q28=makeQuery(id+"F12.imprint","IMPRINT",FACE,{"disambiguationData":[TD([[makeQuery(id+"F12.imprint","IMPRINT",EDGE,{"disambiguationData":[TD([[subQ2,-1.0]])],"derivedFrom":subQ1}),1.0]])]});}
            var Q29;
            {var subQ0=sQuery(id+"F12.wireOp",EDGE,"E29");var subQ1=sQuery(id+"F12.wireOp",EDGE,"E6");var subQ2=makeQuery(id+"F12.imprint","INTERSECT",VERTEX,{"derivedFrom":[subQ1,subQ0]});Q29=makeQuery(id+"F12.imprint","IMPRINT",FACE,{"disambiguationData":[TD([[makeQuery(id+"F12.imprint","IMPRINT",EDGE,{"disambiguationData":[TD([[subQ2,-1.0]])],"derivedFrom":subQ1}),1.0]])]});}
            var Q30;
            {var subQ0=sQuery(id+"F12.wireOp",EDGE,"E12");var subQ1=sQuery(id+"F12.wireOp",EDGE,"E6");var subQ2=makeQuery(id+"F12.imprint","INTERSECT",VERTEX,{"derivedFrom":[subQ1,subQ0]});Q30=makeQuery(id+"F12.imprint","IMPRINT",FACE,{"disambiguationData":[TD([[makeQuery(id+"F12.imprint","IMPRINT",EDGE,{"disambiguationData":[TD([[subQ2,-1.0]])],"derivedFrom":subQ1}),1.0]])]});}
            var Q31;
            {var subQ0=sQuery(id+"F12.wireOp",EDGE,"E30");var subQ1=sQuery(id+"F12.wireOp",EDGE,"E6");var subQ2=makeQuery(id+"F12.imprint","INTERSECT",VERTEX,{"derivedFrom":[subQ1,subQ0]});Q31=makeQuery(id+"F12.imprint","IMPRINT",FACE,{"disambiguationData":[TD([[makeQuery(id+"F12.imprint","IMPRINT",EDGE,{"disambiguationData":[TD([[subQ2,-1.0]])],"derivedFrom":subQ1}),1.0]])]});}
            var Q32;
            {var subQ0=sQuery(id+"F12.wireOp",EDGE,"E19");var subQ1=sQuery(id+"F12.wireOp",EDGE,"E6");var subQ2=makeQuery(id+"F12.imprint","INTERSECT",VERTEX,{"derivedFrom":[subQ1,subQ0]});Q32=makeQuery(id+"F12.imprint","IMPRINT",FACE,{"disambiguationData":[TD([[makeQuery(id+"F12.imprint","IMPRINT",EDGE,{"disambiguationData":[TD([[subQ2,-1.0]])],"derivedFrom":subQ1}),1.0]])]});}
            var Q33;
            {var subQ0=sQuery(id+"F12.wireOp",EDGE,"E31");var subQ1=sQuery(id+"F12.wireOp",EDGE,"E6");var subQ2=makeQuery(id+"F12.imprint","INTERSECT",VERTEX,{"derivedFrom":[subQ1,subQ0]});Q33=makeQuery(id+"F12.imprint","IMPRINT",FACE,{"disambiguationData":[TD([[makeQuery(id+"F12.imprint","IMPRINT",EDGE,{"disambiguationData":[TD([[subQ2,-1.0]])],"derivedFrom":subQ1}),1.0]])]});}
            var Q34;
            {var subQ0=sQuery(id+"F12.wireOp",EDGE,"E10");var subQ1=sQuery(id+"F12.wireOp",EDGE,"E6");var subQ2=makeQuery(id+"F12.imprint","INTERSECT",VERTEX,{"derivedFrom":[subQ1,subQ0]});Q34=makeQuery(id+"F12.imprint","IMPRINT",FACE,{"disambiguationData":[TD([[makeQuery(id+"F12.imprint","IMPRINT",EDGE,{"disambiguationData":[TD([[subQ2,-1.0]])],"derivedFrom":subQ1}),1.0]])]});}
            var Q35;
            {var subQ0=sQuery(id+"F12.wireOp",EDGE,"E37");var subQ1=sQuery(id+"F12.wireOp",EDGE,"E6");var subQ2=makeQuery(id+"F12.imprint","INTERSECT",VERTEX,{"derivedFrom":[subQ1,subQ0]});Q35=makeQuery(id+"F12.imprint","IMPRINT",FACE,{"disambiguationData":[TD([[makeQuery(id+"F12.imprint","IMPRINT",EDGE,{"disambiguationData":[TD([[subQ2,-1.0]])],"derivedFrom":subQ1}),1.0]])]});}
            var Q36;
            {var subQ0=sQuery(id+"F12.wireOp",EDGE,"E38");var subQ1=sQuery(id+"F12.wireOp",EDGE,"E6");var subQ2=makeQuery(id+"F12.imprint","INTERSECT",VERTEX,{"derivedFrom":[subQ1,subQ0]});Q36=makeQuery(id+"F12.imprint","IMPRINT",FACE,{"disambiguationData":[TD([[makeQuery(id+"F12.imprint","IMPRINT",EDGE,{"disambiguationData":[TD([[subQ2,-1.0]])],"derivedFrom":subQ1}),1.0]])]});}
            var Q37;
            {var subQ0=sQuery(id+"F12.wireOp",EDGE,"E20");var subQ1=sQuery(id+"F12.wireOp",EDGE,"E6");var subQ2=makeQuery(id+"F12.imprint","INTERSECT",VERTEX,{"derivedFrom":[subQ1,subQ0]});Q37=makeQuery(id+"F12.imprint","IMPRINT",FACE,{"disambiguationData":[TD([[makeQuery(id+"F12.imprint","IMPRINT",EDGE,{"disambiguationData":[TD([[subQ2,-1.0]])],"derivedFrom":subQ1}),1.0]])]});}
            var Q38;
            {var subQ0=sQuery(id+"F12.wireOp",EDGE,"E36");var subQ1=sQuery(id+"F12.wireOp",EDGE,"E6");var subQ2=makeQuery(id+"F12.imprint","INTERSECT",VERTEX,{"derivedFrom":[subQ1,subQ0]});Q38=makeQuery(id+"F12.imprint","IMPRINT",FACE,{"disambiguationData":[TD([[makeQuery(id+"F12.imprint","IMPRINT",EDGE,{"disambiguationData":[TD([[subQ2,-1.0]])],"derivedFrom":subQ1}),1.0]])]});}
            var Q39;
            {var subQ0=sQuery(id+"F12.wireOp",EDGE,"E14");var subQ1=sQuery(id+"F12.wireOp",EDGE,"E6");var subQ2=makeQuery(id+"F12.imprint","INTERSECT",VERTEX,{"derivedFrom":[subQ1,subQ0]});Q39=makeQuery(id+"F12.imprint","IMPRINT",FACE,{"disambiguationData":[TD([[makeQuery(id+"F12.imprint","IMPRINT",EDGE,{"disambiguationData":[TD([[subQ2,-1.0]])],"derivedFrom":subQ1}),1.0]])]});}
            var Q40;
            {var subQ0=sQuery(id+"F12.wireOp",EDGE,"E35");var subQ1=sQuery(id+"F12.wireOp",EDGE,"E6");var subQ2=makeQuery(id+"F12.imprint","INTERSECT",VERTEX,{"derivedFrom":[subQ1,subQ0]});Q40=makeQuery(id+"F12.imprint","IMPRINT",FACE,{"disambiguationData":[TD([[makeQuery(id+"F12.imprint","IMPRINT",EDGE,{"disambiguationData":[TD([[subQ2,-1.0]])],"derivedFrom":subQ1}),1.0]])]});}
            var Q41;
            {var subQ0=sQuery(id+"F12.wireOp",EDGE,"E22");var subQ1=sQuery(id+"F12.wireOp",EDGE,"E6");var subQ2=makeQuery(id+"F12.imprint","INTERSECT",VERTEX,{"derivedFrom":[subQ1,subQ0]});Q41=makeQuery(id+"F12.imprint","IMPRINT",FACE,{"disambiguationData":[TD([[makeQuery(id+"F12.imprint","IMPRINT",EDGE,{"disambiguationData":[TD([[subQ2,-1.0]])],"derivedFrom":subQ1}),1.0]])]});}
            var Q42;
            {var subQ0=sQuery(id+"F12.wireOp",EDGE,"E23");var subQ1=sQuery(id+"F12.wireOp",EDGE,"E6");var subQ2=makeQuery(id+"F12.imprint","INTERSECT",VERTEX,{"derivedFrom":[subQ1,subQ0]});Q42=makeQuery(id+"F12.imprint","IMPRINT",FACE,{"disambiguationData":[TD([[makeQuery(id+"F12.imprint","IMPRINT",EDGE,{"disambiguationData":[TD([[subQ2,-1.0]])],"derivedFrom":subQ1}),1.0]])]});}
            var Q43;
            {var subQ0=sQuery(id+"F12.wireOp",EDGE,"E11");var subQ1=sQuery(id+"F12.wireOp",EDGE,"E6");var subQ2=makeQuery(id+"F12.imprint","INTERSECT",VERTEX,{"derivedFrom":[subQ1,subQ0]});Q43=makeQuery(id+"F12.imprint","IMPRINT",FACE,{"disambiguationData":[TD([[makeQuery(id+"F12.imprint","IMPRINT",EDGE,{"disambiguationData":[TD([[subQ2,-1.0]])],"derivedFrom":subQ1}),1.0]])]});}
            var Q44;
            {var subQ0=sQuery(id+"F12.wireOp",EDGE,"E33");var subQ1=sQuery(id+"F12.wireOp",EDGE,"E6");var subQ2=makeQuery(id+"F12.imprint","INTERSECT",VERTEX,{"derivedFrom":[subQ1,subQ0]});Q44=makeQuery(id+"F12.imprint","IMPRINT",FACE,{"disambiguationData":[TD([[makeQuery(id+"F12.imprint","IMPRINT",EDGE,{"disambiguationData":[TD([[subQ2,-1.0]])],"derivedFrom":subQ1}),1.0]])]});}
            var Q45;
            {var subQ0=sQuery(id+"F12.wireOp",EDGE,"E21");var subQ1=sQuery(id+"F12.wireOp",EDGE,"E6");var subQ2=makeQuery(id+"F12.imprint","INTERSECT",VERTEX,{"derivedFrom":[subQ1,subQ0]});Q45=makeQuery(id+"F12.imprint","IMPRINT",FACE,{"disambiguationData":[TD([[makeQuery(id+"F12.imprint","IMPRINT",EDGE,{"disambiguationData":[TD([[subQ2,-1.0]])],"derivedFrom":subQ1}),1.0]])]});}
            var Q46;
            {var subQ0=sQuery(id+"F12.wireOp",EDGE,"E34");var subQ1=sQuery(id+"F12.wireOp",EDGE,"E6");var subQ2=makeQuery(id+"F12.imprint","INTERSECT",VERTEX,{"derivedFrom":[subQ1,subQ0]});Q46=makeQuery(id+"F12.imprint","IMPRINT",FACE,{"disambiguationData":[TD([[makeQuery(id+"F12.imprint","IMPRINT",EDGE,{"disambiguationData":[TD([[subQ2,-1.0]])],"derivedFrom":subQ1}),1.0]])]});}
            var Q47;
            {var subQ0=sQuery(id+"F12.wireOp",EDGE,"E9");var subQ1=sQuery(id+"F12.wireOp",EDGE,"E6");var subQ2=makeQuery(id+"F12.imprint","INTERSECT",VERTEX,{"derivedFrom":[subQ1,subQ0]});Q47=makeQuery(id+"F12.imprint","IMPRINT",FACE,{"disambiguationData":[TD([[makeQuery(id+"F12.imprint","IMPRINT",EDGE,{"disambiguationData":[TD([[subQ2,-1.0]])],"derivedFrom":subQ1}),1.0]])]});}
            extrude(context, id + "F13", {"entities" : qUnion([Q0, Q1, Q2, Q3, Q4, Q5, Q6, Q7, Q8, Q9, Q10, Q11, Q12, Q13, Q14, Q15, Q16, Q17, Q18, Q19, Q20, Q21, Q22, Q23, Q24, Q25, Q26, Q27, Q28, Q29, Q30, Q31, Q32, Q33, Q34, Q35, Q36, Q37, Q38, Q39, Q40, Q41, Q42, Q43, Q44, Q45, Q46, Q47]), "operationType" : NewBodyOperationType.REMOVE, "oppositeDirection" : true, "depth" : 3.17 * mm, "offsetDistance" : 25.4 * mm});
        }
        {
            var Q0;
            Q0=makeQuery(id+"F13.boolean.opBoolean","COPY",FACE,{"derivedFrom":makeQuery(id+"F13.opExtrude","CAP_FACE",FACE,{"disambiguationData":[OSD([sQuery(id+"F10.wireOp",EDGE,"E4"),sQuery(id+"F12.wireOp",EDGE,"E6"),sQuery(id+"F12.wireOp",EDGE,"E23"),sQuery(id+"F12.wireOp",EDGE,"E24"),sQuery(id+"F12.wireOp",EDGE,"E25"),sQuery(id+"F12.wireOp",EDGE,"E26"),sQuery(id+"F12.wireOp",EDGE,"E27"),sQuery(id+"F12.wireOp",EDGE,"E28"),sQuery(id+"F12.wireOp",EDGE,"E29"),sQuery(id+"F12.wireOp",EDGE,"E30"),sQuery(id+"F12.wireOp",EDGE,"E31"),sQuery(id+"F12.wireOp",EDGE,"E32"),sQuery(id+"F12.wireOp",EDGE,"E33"),sQuery(id+"F12.wireOp",EDGE,"E34"),sQuery(id+"F12.wireOp",EDGE,"E35"),sQuery(id+"F12.wireOp",EDGE,"E36"),sQuery(id+"F12.wireOp",EDGE,"E37"),sQuery(id+"F12.wireOp",EDGE,"E38")])],"isStart":false})});
            var sketch = newSketch(context, id + "F14", { "sketchPlane" : qUnion([Q0])});
            skCircle(sketch, "E39", {"center": v(0, 0) * mm, "radius": 9.53 * mm});
            skSolve(sketch);
        }
        {
            var Q0;
            Q0=qSketchRegion(id+"F14",true);
            extrude(context, id + "F15", {"entities" : qUnion([Q0]), "operationType" : NewBodyOperationType.REMOVE, "oppositeDirection" : true, "depth" : 3.17 * mm, "offsetDistance" : 25.4 * mm});
        }
    });
